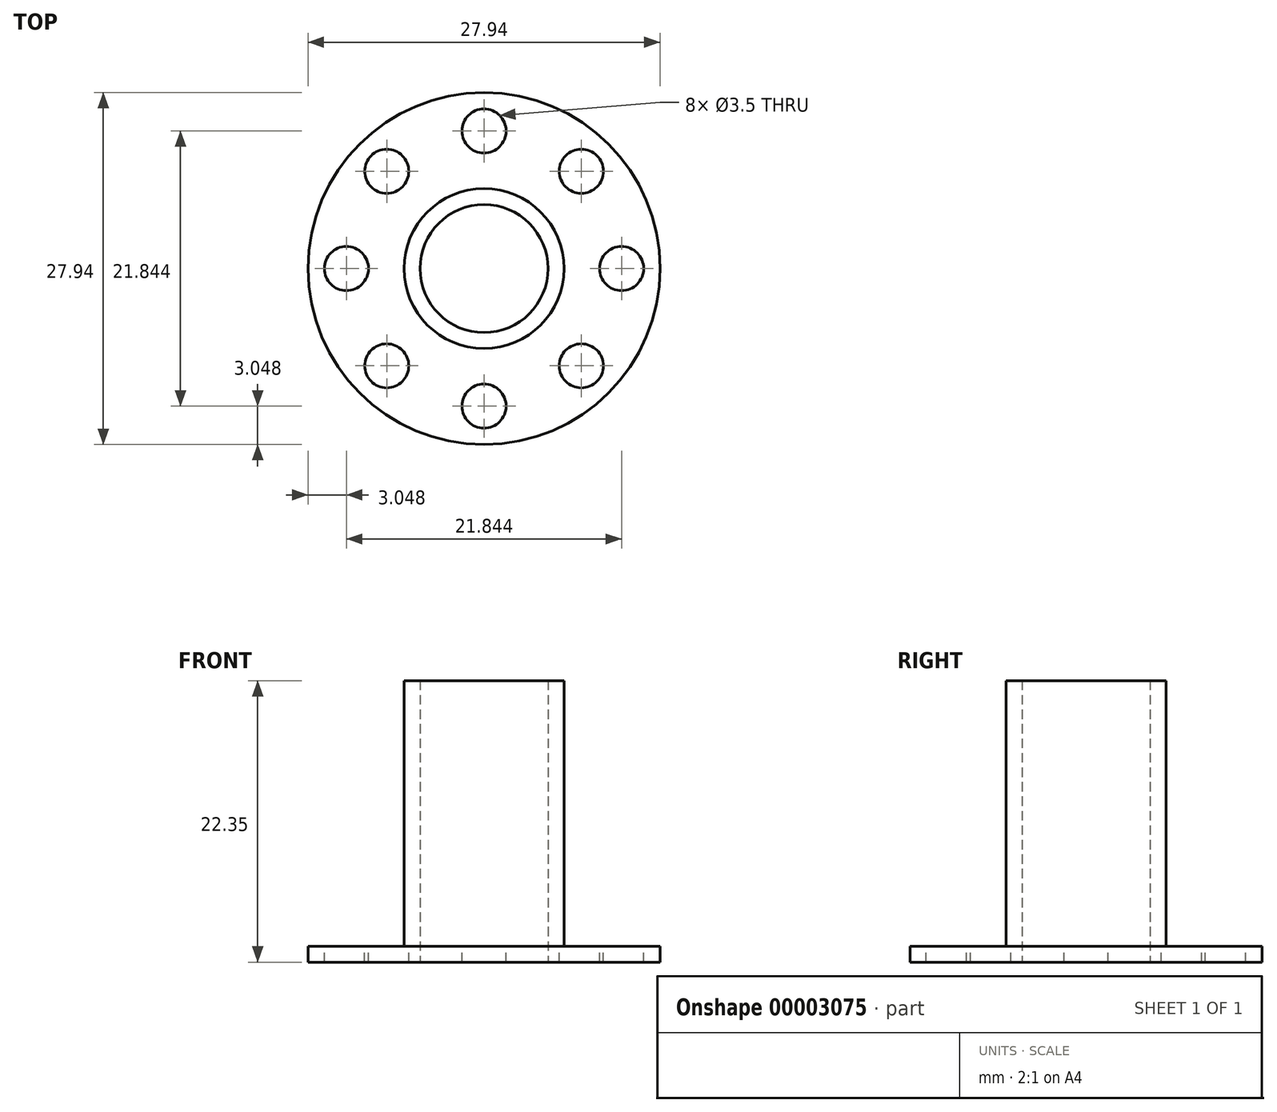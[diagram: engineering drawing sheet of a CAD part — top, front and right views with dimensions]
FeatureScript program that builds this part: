
annotation { "Feature Type Name" : "Feature", "Feature Type Description" : "" }
export const myFeature = defineFeature(function(context is Context, id is Id, definition is map)
    precondition{}
    {
        {
            var Q0;
            Q0=qCreatedBy(makeId("Top.planeOp"),FACE);
            var sketch = newSketch(context, id + "F0", { "sketchPlane" : qUnion([Q0])});
            skCircle(sketch, "E0", {"center": v(0, 0) * mm, "radius": 13.97 * mm});
            skCircle(sketch, "E1", {"center": v(0, 0) * mm, "radius": 5.08 * mm});
            skSolve(sketch);
        }
        {
            var Q0;
            Q0=makeQuery(id+"F0.imprint","IMPRINT",FACE,{"disambiguationData":[TD([[makeQuery(id+"F0.imprint","IMPRINT",EDGE,{"derivedFrom":sQuery(id+"F0.wireOp",EDGE,"E0")}),1.0]])]});
            extrude(context, id + "F1", {"entities" : qUnion([Q0]), "depth" : 1.27 * mm});
        }
        {
            var Q0;
            Q0=makeQuery(id+"F1.opExtrude","CAP_FACE",FACE,{"disambiguationData":[OSD([sQuery(id+"F0.wireOp",EDGE,"E0"),sQuery(id+"F0.wireOp",EDGE,"E1")])],"isStart":false});
            var sketch = newSketch(context, id + "F2", { "sketchPlane" : qUnion([Q0])});
            skCircle(sketch, "E2", {"center": v(0, 0) * mm, "radius": 6.35 * mm});
            skCircle(sketch, "E3", {"center": v(0, 0) * mm, "radius": 5.08 * mm});
            skSolve(sketch);
        }
        {
            var Q0;
            Q0=makeQuery(id+"F2.imprint","IMPRINT",FACE,{"disambiguationData":[TD([[makeQuery(id+"F2.imprint","IMPRINT",EDGE,{"derivedFrom":sQuery(id+"F2.wireOp",EDGE,"E2")}),1.0]])]});
            extrude(context, id + "F3", {"entities" : qUnion([Q0]), "operationType" : NewBodyOperationType.ADD, "depth" : 21.08 * mm});
        }
        {
            var Q0;
            Q0=makeQuery(id+"F1.opExtrude","CAP_FACE",FACE,{"disambiguationData":[OSD([sQuery(id+"F0.wireOp",EDGE,"E0"),sQuery(id+"F0.wireOp",EDGE,"E1")])],"isStart":false});
            var sketch = newSketch(context, id + "F4", { "sketchPlane" : qUnion([Q0])});
            skCircle(sketch, "E4", {"center": v(0, 10.92) * mm, "radius": 1.75 * mm});
            skSolve(sketch);
        }
        {
            var Q0;
            Q0=makeQuery(id+"F4.imprint","IMPRINT",FACE,{"disambiguationData":[TD([[makeQuery(id+"F4.imprint","IMPRINT",EDGE,{"derivedFrom":sQuery(id+"F4.wireOp",EDGE,"E4")}),1.0]])]});
            extrude(context, id + "F5", {"entities" : qUnion([Q0]), "operationType" : NewBodyOperationType.REMOVE, "endBound" : BoundingType.THROUGH_ALL, "oppositeDirection" : true, "depth" : 25.4 * mm});
        }
        {
            var Q0;
            Q0=qCreatedBy(makeId("Front.planeOp"),FACE);
            var sketch = newSketch(context, id + "F6", { "sketchPlane" : qUnion([Q0])});
            skLineSegment(sketch, "E5", {"start": v(0, 0) * mm, "end": v(0, 27.1) * mm, "construction": true});
            skSolve(sketch);
        }
        {
            var Q0;
            Q0=makeQuery(id+"F5.boolean.opBoolean","COPY",FACE,{"derivedFrom":makeQuery(id+"F5.opExtrude","SWEPT_FACE",FACE,{"disambiguationData":[OSD([sQuery(id+"F4.wireOp",EDGE,"E4")])]})});
            var Q1;
            Q1=sQuery(id+"F6.wireOp",EDGE,"E5");
            circularPattern(context, id + "F7", {"faces" : qUnion([Q0]), "axis" : qUnion([Q1]), "angle" : 360 / 8 * degree, "instanceCount" : 8, "patternType" : PatternType.FACE});
        }
    });
